# Revit family: 88619085
name_source: partatom
category: Plumbing Fixtures
units: mm (PartAtom-declared; Revit-internal decimal feet)

## family parameters
Always vertical = Yes
Cut with Voids When Loaded = No
OmniClass Number = 23.45.55.00
OmniClass Title = Sanitary Faucets, Wastes
Part Type = Normal
Room Calculation Point = No
Round Connector Dimension = Use Diameter
Shared = No
Work Plane-Based = No

## types (1)
- 88619085 Cover part for shower faucet
    2D/3D/BIM Files URL = http://static.hansa.com
    3D View = https://static.hansa.com
    Additional Features = protected against back-flow in domestic use (according to DIN EN 1717)
Safety lock against scalding 38°C (36°-44°)
    Advanced Features = Thermal disinfection without cartridge readjustment
    Ambience photo = http://static.hansa.com
    Approval ABP = PA-IX 38187/IC
    Approval DVGW = DW-6509CS0197
    AssetType = Fixed
    BIMObjectName = 88619085
    Backflow Prevention EN1717 = EB
    BodyMaterial = Brass
    Brand = HANSA
    CO2 Emissions (A1-A3) = 26.92
    CO2 Emissions (A4) = 0.44
    CO2 Emissions (B7) = 4400.4
    CO2 Emissions (C2) = 0.02
    CO2 Emissions (C3) = 0.02
    CO2 Emissions (C4) = 0.35
    CO2 Emissions (D) = -8.33
    Catalog Drawing URL = http://static.hansa.com
    CloseOffRating = 0
    Color = Chrome
    Concealed Parts = Round rosette;Function unit;BLUECLICK for an easy, screwless trim plate installation;BLUETUNE alignment after installation of +/- 3,5º
    DN Size = 170 mm
    Default Elevation = 0 mm  [stored 0 ft]
    Dimension Drawing URL = http://static.hansa.com
    DurationUnit = Year
    EAN Number = 4057304012532
    EN Standard = EN 1111
    ETIM Class Number = EC010546 Mechanical control system for shower
    FDV Document URL = http://www.hansa.com
    FaucetMainMaterial = Chrome
    Features = Trim Kit;Thermostatic
    Finish = Polished
    Flow Drawing URL = http://static.hansa.com
    Flow Rate At 300kPa = 0.4 L/s
    FlowCoefficient = 0
    Group = Shower faucet
    IfcExportAs = IfcValveType
    IfcExportType = FAUCET
    Installation Type = Concealed wall mounting
    Installation and Maintenance Guide URL = http://static.hansa.com
    Interactive AR View URL = https://static.hansa.com
    Lever Handle = Temperature control handle;Flow control handle
    Manufacturer = HANSA
    ManufacturerName = HANSA
    ManufacturerURL = http://www.hansa.com
    Market = International;Germany;Austria;Switzerland;Belgium;Netherlands;France;Czech Republic;Slovakia;Hungary;Romania;Italy;Spain;Greece;Portugal;Australia
    Material = Brass
    Max. Hot Water Supply = 80 °C
    Mechanical Parts = Ceramic head part for flow control;Thermostatic cartridge for automatic temperature control;Non-return valve(s)
    Mobile Product Information URL = http://mpi.hansa.com
    Model = 88619085 Cover part for shower faucet
    ModelReference = 88619085
    NBSDescription = Shower mixers
    NBSReference = 45-35-70/335
    Name = 88619085 Cover part for shower faucet
    Name_en = 88619085 Cover part for shower faucet
    Noise Class = I (ISO 3822)
    NominalDepth = 71 mm
    NominalHeight = 170 mm  [stored 0.557743 ft]
    NominalWidth = 170 mm  [stored 0.557743 ft]
    Product Code = 88619085
    Product Family = HANSACLINICA Safety+
    Product Image URL = http://static.hansa.com
    Product URL = http://static.hansa.com
    Sales Package dimensions (LxWxH) = 204 x 186 x 174
    Shape = Sculptured
    Size = 170x70x170 mm
    Spare-Part Information URL = http://static.hansa.com
    Surface treatment = Chrome
    Technical DataSheet URL = http://www.hansa.com
    UNSPSC Class Number = 30181810 Faucet trim
    URL ABP = http://static.hansa.com
    URL DVGW = http://static.hansa.com
    URL Declaration Of Performance (DOP) = http://static.hansa.com
    URL Declaration of Asbestos = http://static.hansa.com
    URL Declaration of Conformity = http://static.hansa.com
    URL Declaration of SCIP = http://static.hansa.com
    URL EU Packaging Declaration = http://static.hansa.com
    URL EcoLabel Declaration = http://static.hansa.com
    URL Environmental Product Declaration EPD = http://www.hansa.com Group EPD_Cover part for bath and shower faucet.pdf
    URL Materials Declaration = http://www.hansa.com
    URL REACH = http://static.hansa.com
    Uniclass2 = Pr_40_30_96_78
    Uniclass2015Description = Shower manual water supply sets
    Uniclass2015Reference = Pr_40_20_87_78
    Version = 1
    VersionDate = 20/04/2024
    Warranty Information URL = http://warranty.hansa.com
    WarrantyDescription = http://warranty.hansa.com
    WarrantyDurationUnit = Year
    Working Pressure = 100 - 1000 kPa

note: [stored X ft] marks values corroborated as IEEE doubles in the binary element streams (Revit-internal decimal feet)

## geometry (parser evidence)
native form markers: Sweep x4
no freeform markers — native parametric forms only
